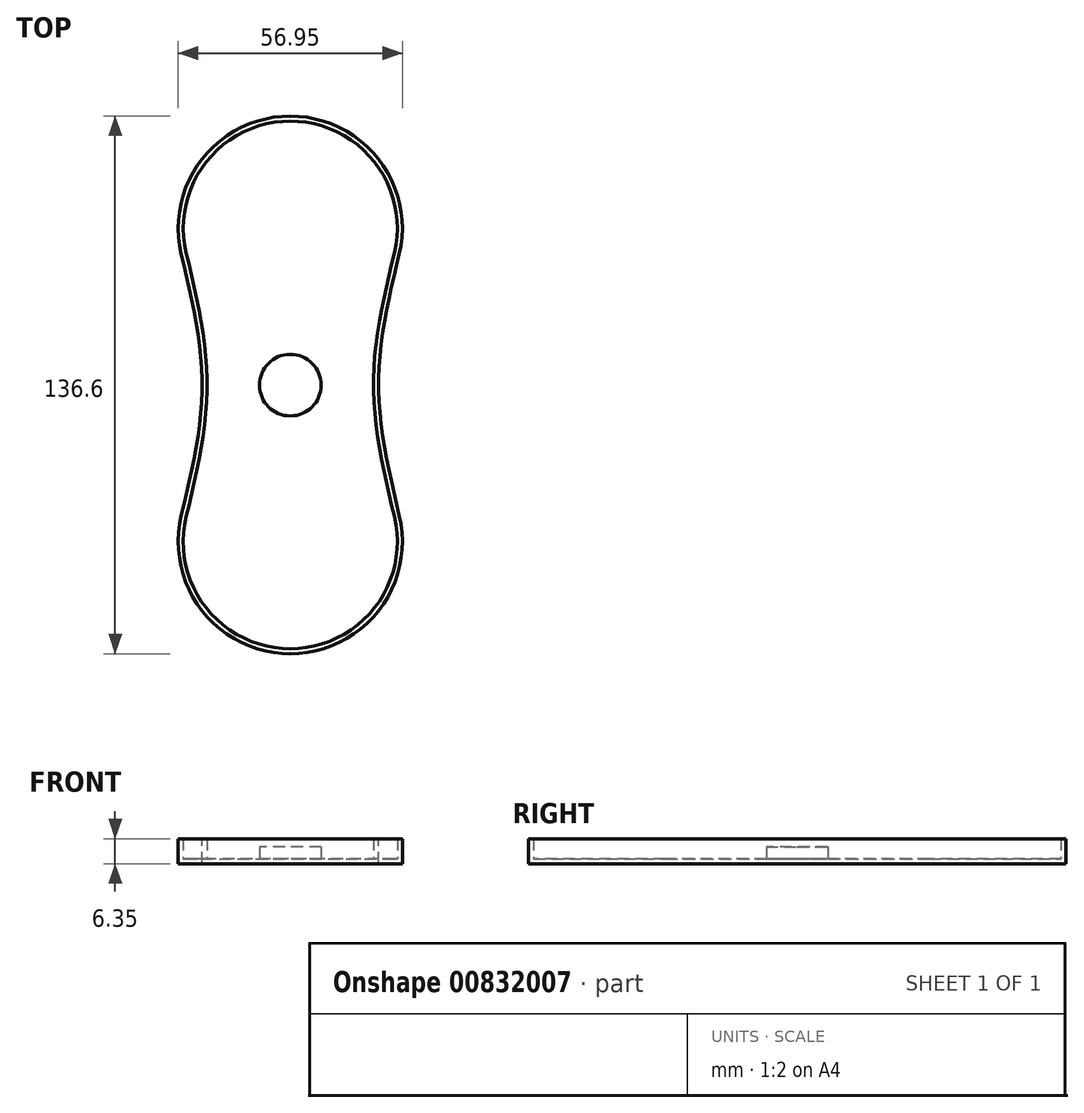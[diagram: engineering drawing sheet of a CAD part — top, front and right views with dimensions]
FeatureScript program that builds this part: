
annotation { "Feature Type Name" : "Feature", "Feature Type Description" : "" }
export const myFeature = defineFeature(function(context is Context, id is Id, definition is map)
    precondition{}
    {
        {
            var Q0;
            Q0=qCreatedBy(makeId("Top.planeOp"),FACE);
            var sketch = newSketch(context, id + "F0", { "sketchPlane" : qUnion([Q0])});
            skFitSpline(sketch, "E0", {"points": [v(0, 0) * mm, v(5.29, 32.99) * mm, v(0, 66.45) * mm], "startDerivative": vector(15.88, 66.08) * mm, "endDerivative": vector(-15.84, 66.82) * mm});
            skFitSpline(sketch, "E1", {"points": [v(55.37, 66.45) * mm, v(50.08, 33.47) * mm, v(55.37, 0) * mm], "startDerivative": vector(-15.88, -66.08) * mm, "endDerivative": vector(15.84, -66.82) * mm});
            skArc(sketch, "E2", {"start": v(0, 66.45) * mm, "mid": v(27.69, 101.47) * mm, "end": v(55.37, 66.45) * mm});
            skArc(sketch, "E3", {"start": v(0, 0) * mm, "mid": v(27.69, -35.13) * mm, "end": v(55.37, 0) * mm});
            skSolve(sketch);
        }
        {
            var Q0;
            Q0=makeQuery(id+"F0.imprint","IMPRINT",FACE,{"disambiguationData":[TD([[makeQuery(id+"F0.imprint","IMPRINT",EDGE,{"derivedFrom":sQuery(id+"F0.wireOp",EDGE,"E0")}),-1.0]])]});
            extrude(context, id + "F1", {"entities" : qUnion([Q0]), "depth" : 6.35 * mm, "offsetDistance" : 25.4 * mm});
        }
        {
            var Q0;
            Q0=makeQuery(id+"F1.opExtrude","CAP_FACE",FACE,{"disambiguationData":[OSD([sQuery(id+"F0.wireOp",EDGE,"E0"),sQuery(id+"F0.wireOp",EDGE,"E1"),sQuery(id+"F0.wireOp",EDGE,"E2"),sQuery(id+"F0.wireOp",EDGE,"E3")])],"isStart":false});
            shell(context, id + "F2", {"entities" : qUnion([Q0]), "thickness" : 1.27 * mm});
        }
        {
            var Q0;
            Q0=makeQuery(id+"F2.opShell","OFFSET_FACE",FACE,{"disambiguationData":[OSD([sQuery(id+"F0.wireOp",EDGE,"E0"),sQuery(id+"F0.wireOp",EDGE,"E1"),sQuery(id+"F0.wireOp",EDGE,"E2"),sQuery(id+"F0.wireOp",EDGE,"E3")])]});
            var sketch = newSketch(context, id + "F3", { "sketchPlane" : qUnion([Q0])});
            skCircle(sketch, "E4", {"center": v(27.69, 33.13) * mm, "radius": 7.83 * mm});
            skPoint(sketch, "E4.centerSnap0", {"position": v(27.69, -33.86) * mm});
            skSolve(sketch);
        }
        {
            var Q0;
            Q0=makeQuery(id+"F3.imprint","IMPRINT",FACE,{"disambiguationData":[TD([[makeQuery(id+"F3.imprint","IMPRINT",EDGE,{"derivedFrom":sQuery(id+"F3.wireOp",EDGE,"E4")}),1.0]])]});
            extrude(context, id + "F4", {"entities" : qUnion([Q0]), "operationType" : NewBodyOperationType.ADD, "depth" : 3.05 * mm, "offsetDistance" : 25.4 * mm});
        }
    });
